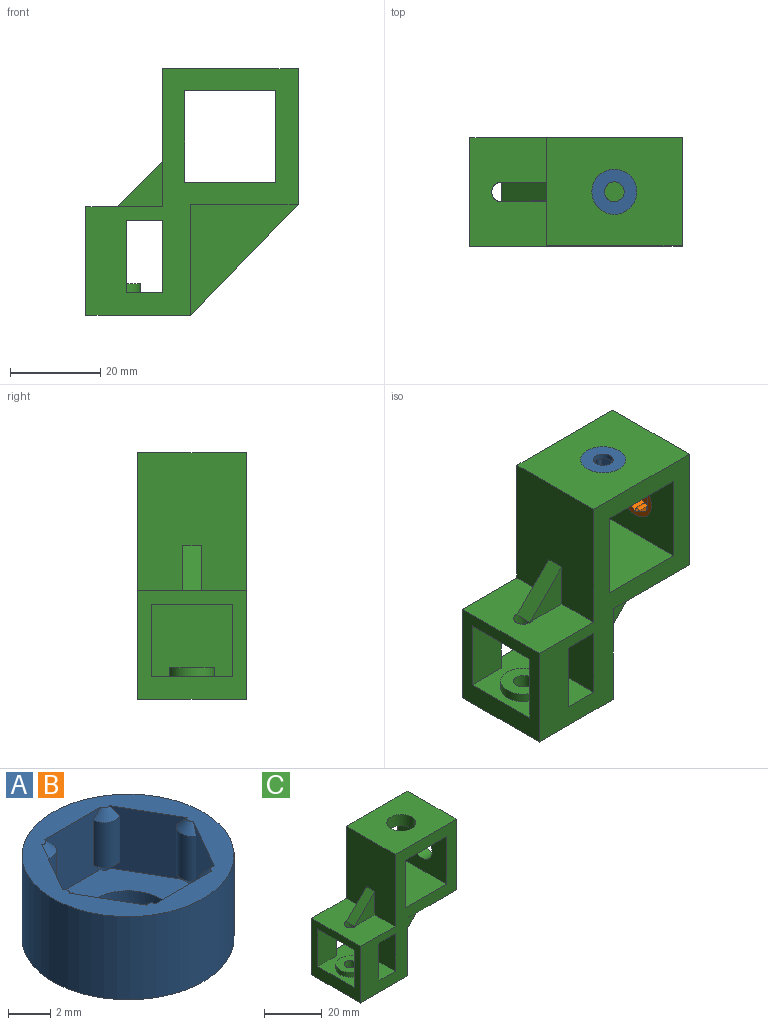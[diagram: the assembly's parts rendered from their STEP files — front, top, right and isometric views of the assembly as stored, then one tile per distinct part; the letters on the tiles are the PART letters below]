
ASSEMBLY  parts=3 mates=2
PART A: 29 faces, bbox 10x10x4.8 mm
  f0: plane 3.77x3.6mm, normal (0,-1,0), area 10.5mm2, adj f7,f8,f9,f10,f17,f18,f19,f26
  f1: plane 3.6x3.27mm, normal (-0.87,-0.5,0), area 10.5mm2, adj f7,f8,f9,f10,f14,f15,f16,f26
  f2: plane 3.6x3.27mm, normal (-0.87,0.5,0), area 10.5mm2, adj f7,f11,f12,f13,f14,f15,f16,f26
  f3: plane 3.77x3.6mm, normal (0,1,0), area 10.5mm2, adj f7,f11,f12,f13,f23,f24,f25,f26
  f4: plane 3.6x3.27mm, normal (0.87,0.5,0), area 10.5mm2, adj f7,f20,f21,f22,f23,f24,f25,f26
  f5: cylinder r=5mm len=10mm, axis (0,0,-1), area 150.8mm2, adj f7,f27
  f6: plane 3.6x3.27mm, normal (0.87,-0.5,0), area 10.5mm2, adj f7,f17,f18,f19,f20,f21,f22,f26
  f7: plane 10x10mm, normal (0,0,1), area 31.5mm2, adj f0,f1,f2,f3,f4,f5,f6,f9
  f8: cylinder r=0.75mm len=2.6mm, axis (0,0,-1), area 4.1mm2, adj f0,f1,f9,f10
  f9: cone r=0.25mm half-angle=45deg, axis (0,0,-1), area 0.7mm2, adj f0,f1,f7,f8
  f10: cone r=0.75mm half-angle=45deg, axis (0,0,1), area 0.7mm2, adj f0,f1,f8,f26
  f11: cylinder r=0.75mm len=2.6mm, axis (0,0,-1), area 4.1mm2, adj f2,f3,f12,f13
  f12: cone r=0.25mm half-angle=45deg, axis (0,0,-1), area 0.7mm2, adj f2,f3,f7,f11
  f13: cone r=0.75mm half-angle=45deg, axis (0,0,1), area 0.7mm2, adj f2,f3,f11,f26
  f14: cylinder r=0.75mm len=2.6mm, axis (0,0,-1), area 4.1mm2, adj f1,f2,f15,f16
  f15: cone r=0.25mm half-angle=45deg, axis (0,0,-1), area 0.7mm2, adj f1,f2,f7,f14
  f16: cone r=0.75mm half-angle=45deg, axis (0,0,1), area 0.7mm2, adj f1,f2,f14,f26
  f17: cone r=0.75mm half-angle=45deg, axis (0,0,1), area 0.7mm2, adj f0,f6,f19,f26
  f18: cone r=0.25mm half-angle=45deg, axis (0,0,-1), area 0.7mm2, adj f0,f6,f7,f19
  f19: cylinder r=0.75mm len=2.6mm, axis (0,0,-1), area 4.1mm2, adj f0,f6,f17,f18
  f20: cone r=0.75mm half-angle=45deg, axis (0,0,1), area 0.7mm2, adj f4,f6,f22,f26
  f21: cone r=0.25mm half-angle=45deg, axis (0,0,-1), area 0.7mm2, adj f4,f6,f7,f22
  f22: cylinder r=0.75mm len=2.6mm, axis (0,0,-1), area 4.1mm2, adj f4,f6,f20,f21
  f23: cylinder r=0.75mm len=2.6mm, axis (0,0,-1), area 4.1mm2, adj f3,f4,f24,f25
  f24: cone r=0.25mm half-angle=45deg, axis (0,0,-1), area 0.7mm2, adj f3,f4,f7,f23
  f25: cone r=0.75mm half-angle=45deg, axis (0,0,1), area 0.7mm2, adj f3,f4,f23,f26
  f26: plane 8.29x7.4mm, normal (0,0,1), area 31.8mm2, adj f0,f1,f2,f3,f4,f6,f10,f13
  f27: plane 10x10mm, normal (0,0,-1), area 63.3mm2, adj f5,f28
  f28: cylinder r=2.2mm len=4.4mm, axis (0,0,-1), area 16.6mm2, adj f26,f27
PART B: same geometry as A
PART C: 37 faces, bbox 47x24x54.6 mm
  f0: plane 30.6x24mm, normal (-1,0,0), area 694.4mm2, adj f5,f6,f7,f21,f22,f23,f24
  f1: plane 4x2mm, normal (0,0,-1), area 7.1mm2, adj f21,f22,f23,f35,f36
  f2: plane 24x16mm, normal (-1,0,0), area 384mm2, adj f5,f6,f25,f32
  f3: plane 23.84x10mm, normal (0,0,-1), area 238.4mm2, adj f6,f9,f17,f19
  f4: plane 24.6x10mm, normal (1,0,0), area 246mm2, adj f5,f8,f16,f20
  f5: plane 54.6x47mm, normal (0,1,0), area 923.4mm2, adj f0,f2,f4,f7,f8,f9,f10,f11
  f6: plane 54.6x47mm, normal (0,-1,0), area 923.4mm2, adj f0,f2,f3,f7,f9,f10,f11,f12
  f7: plane 30x24mm, normal (0,0,1), area 641.5mm2, adj f0,f5,f6,f9,f14
  f8: plane 23.84x10mm, normal (0,0,-1), area 238.4mm2, adj f4,f5,f9,f20
  f9: plane 30x24mm, normal (1,0,0), area 641.5mm2, adj f3,f5,f6,f7,f8,f15,f18
  f10: plane 24x20.2mm, normal (0,0,-1), area 406.3mm2, adj f5,f6,f11,f13,f14
  f11: plane 24x20.2mm, normal (-1,0,0), area 406.3mm2, adj f5,f6,f10,f12,f15
  f12: plane 24x20.2mm, normal (0,0,1), area 484.8mm2, adj f5,f6,f11,f13
  f13: plane 24x20.2mm, normal (1,0,0), area 484.8mm2, adj f5,f6,f10,f12
  f14: cylinder r=5mm len=10mm, axis (0,0,1), area 153.9mm2, adj f7,f10
  f15: cylinder r=5mm len=10mm, axis (1,0,0), area 153.9mm2, adj f9,f11
  f16: plane 24x23.16mm, normal (0,0,-1), area 540.6mm2, adj f4,f5,f6,f17,f18,f28,f29
  f17: plane 24.6x10mm, normal (1,0,0), area 246mm2, adj f3,f6,f16,f19
  f18: plane 24.6x23.84mm, normal (0.72,0,-0.7), area 137mm2, adj f9,f16,f19,f20
  f19: plane 24.6x23.84mm, normal (0,-1,0), area 293.3mm2, adj f3,f17,f18
  f20: plane 24.6x23.84mm, normal (0,1,0), area 293.3mm2, adj f4,f8,f18
  f21: plane 10x10mm, normal (-0.71,0,0.71), area 56.6mm2, adj f0,f1,f22,f23
  f22: plane 10x10mm, normal (0,-1,0), area 50mm2, adj f0,f1,f21,f24
  f23: plane 10x10mm, normal (0,1,0), area 50mm2, adj f0,f1,f21,f24
  f24: plane 24x17mm, normal (0,0,1), area 360.2mm2, adj f0,f5,f6,f22,f23,f28,f35
  f25: plane 24x17mm, normal (0,0,1), area 275.5mm2, adj f2,f5,f6,f26,f28,f30,f31,f33
  f26: cylinder r=5mm len=10mm, axis (0,0,1), area 62.8mm2, adj f25,f27
  f27: plane 10x10mm, normal (0,0,1), area 63.3mm2, adj f26,f29
  f28: plane 24x24mm, normal (-1,0,0), area 288mm2, adj f5,f6,f16,f24,f25,f30,f32,f33
  f29: cylinder r=2.2mm len=7mm, axis (0,0,1), area 96.8mm2, adj f16,f27
  f30: plane 16x9mm, normal (0,-1,0), area 144mm2, adj f25,f28,f31,f32
  f31: plane 16x3mm, normal (1,0,0), area 48mm2, adj f5,f25,f30,f32
  f32: plane 24x17mm, normal (0,0,-1), area 339mm2, adj f2,f5,f6,f28,f30,f31,f33,f34
  f33: plane 16x9mm, normal (0,1,0), area 144mm2, adj f25,f28,f32,f34
  f34: plane 16x3mm, normal (1,0,0), area 48mm2, adj f6,f25,f32,f33
  f35: cylinder r=2.2mm len=4.4mm, axis (0,0,1), area 35.8mm2, adj f1,f24,f32,f36
  f36: plane 3x1.83mm, normal (-1,0,0), area 5.5mm2, adj f1,f32,f35
PLACE A rot(axis=(1,0,0),180deg) t=(15,0,13.8)mm
PLACE B rot(axis=(0,-1,0),90deg) t=(28.8,0,0)mm
PLACE C at identity
MATE fastened A.f5 <-> C.f14  axis (0,0,1) through (15,0,15)mm
MATE fastened B.f5 <-> C.f15  axis (1,0,0) through (30,0,0)mm
